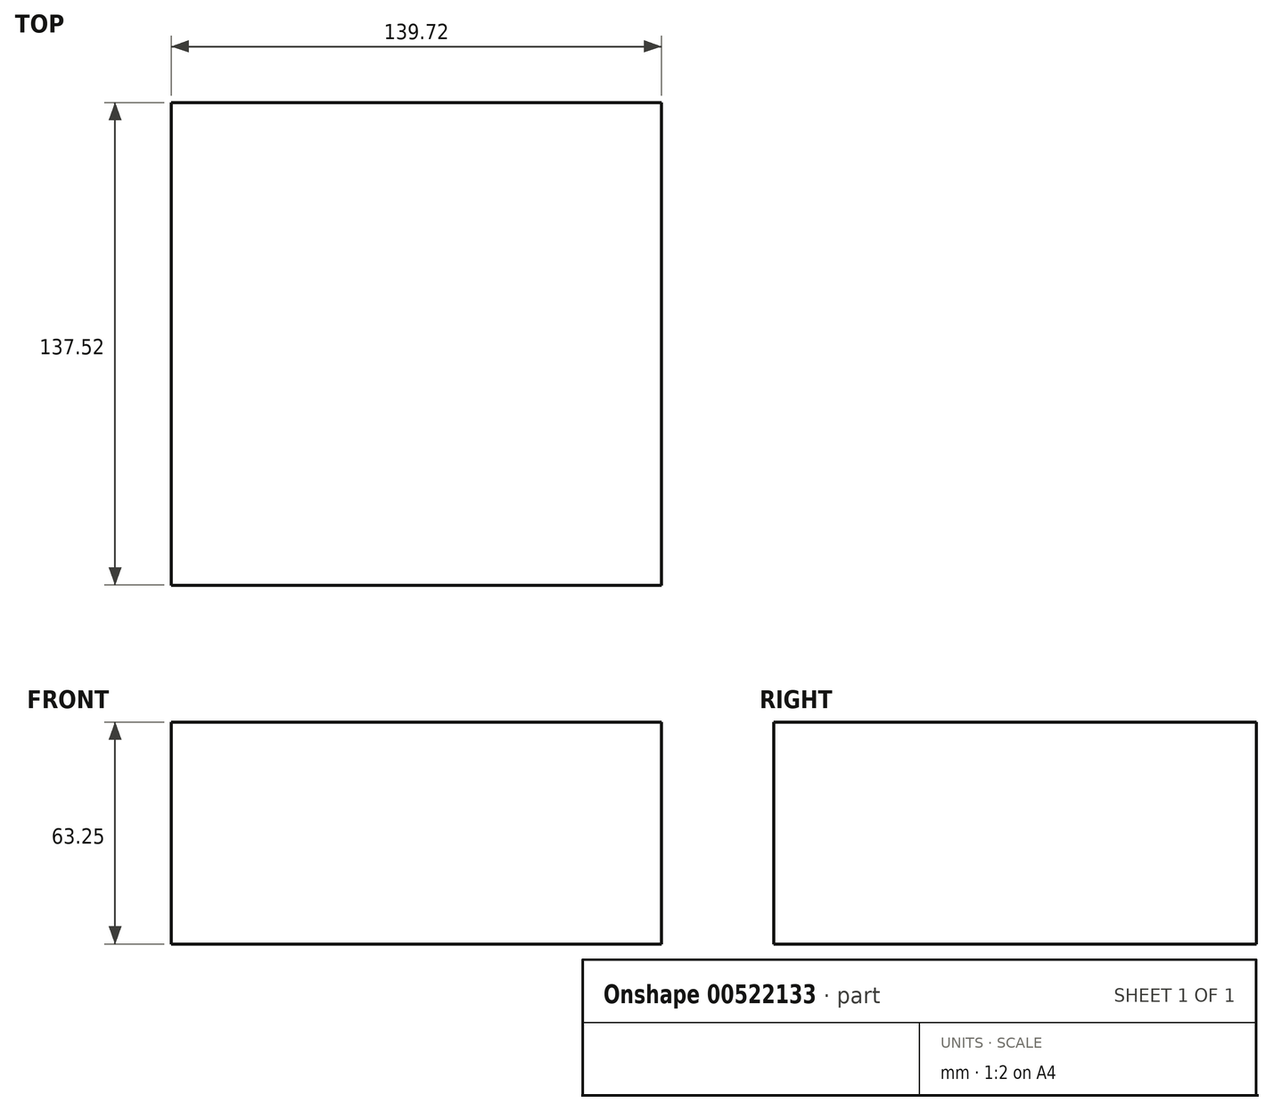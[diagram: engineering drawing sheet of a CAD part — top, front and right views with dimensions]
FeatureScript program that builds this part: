
annotation { "Feature Type Name" : "Feature", "Feature Type Description" : "" }
export const myFeature = defineFeature(function(context is Context, id is Id, definition is map)
    precondition{}
    {
        {
            var Q0;
            Q0=qCreatedBy(makeId("Top.planeOp"),FACE);
            var sketch = newSketch(context, id + "F0", { "sketchPlane" : qUnion([Q0])});
            skLineSegment(sketch, "E0.bottom", {"start": v(69.86, -68.76) * mm, "end": v(-69.86, -68.76) * mm});
            skLineSegment(sketch, "E0.top", {"start": v(69.86, 68.76) * mm, "end": v(-69.86, 68.76) * mm});
            skLineSegment(sketch, "E0.left", {"start": v(69.86, -68.76) * mm, "end": v(69.86, 68.76) * mm});
            skLineSegment(sketch, "E0.right", {"start": v(-69.86, -68.76) * mm, "end": v(-69.86, 68.76) * mm});
            skPoint(sketch, "E0.middle", {"position": v(0, 0) * mm});
            skLineSegment(sketch, "E1", {"start": v(0, 68.76) * mm, "end": v(0, -68.76) * mm});
            skSolve(sketch);
        }
        {
            var Q0;
            Q0=qCreatedBy(makeId("Top.planeOp"),FACE);
            var sketch = newSketch(context, id + "F1", { "sketchPlane" : qUnion([Q0])});
            skCircle(sketch, "E2", {"center": v(54.26, 0) * mm, "radius": 9.82 * mm});
            skSolve(sketch);
        }
        {
            var Q0;
            Q0=sQuery(id+"F1.wireOp",EDGE,"E2");
            var Q1;
            Q1=sQuery(id+"F0.wireOp",EDGE,"E1");
            revolve(context, id + "F2", {"bodyType" : ToolBodyType.SURFACE, "surfaceEntities" : qUnion([Q0]), "axis" : qUnion([Q1]), "revolveType" : RevolveType.ONE_DIRECTION, "angle" : 180 * degree});
        }
        {
            var Q0;
            {var subQ0=sQuery(id+"F0.wireOp",EDGE,"E0.right");Q0=makeQuery(id+"F0.imprint","IMPRINT",FACE,{"disambiguationData":[TD([[makeQuery(id+"F0.imprint","IMPRINT",EDGE,{"derivedFrom":subQ0}),-1.0]])]});}
            var Q1;
            {var subQ0=sQuery(id+"F0.wireOp",EDGE,"E0.left");Q1=makeQuery(id+"F0.imprint","IMPRINT",FACE,{"disambiguationData":[TD([[makeQuery(id+"F0.imprint","IMPRINT",EDGE,{"derivedFrom":subQ0}),1.0]])]});}
            extrude(context, id + "F3", {"entities" : qUnion([Q0, Q1]), "oppositeDirection" : true, "depth" : 63.25 * mm, "offsetDistance" : 25.4 * mm});
        }
    });
